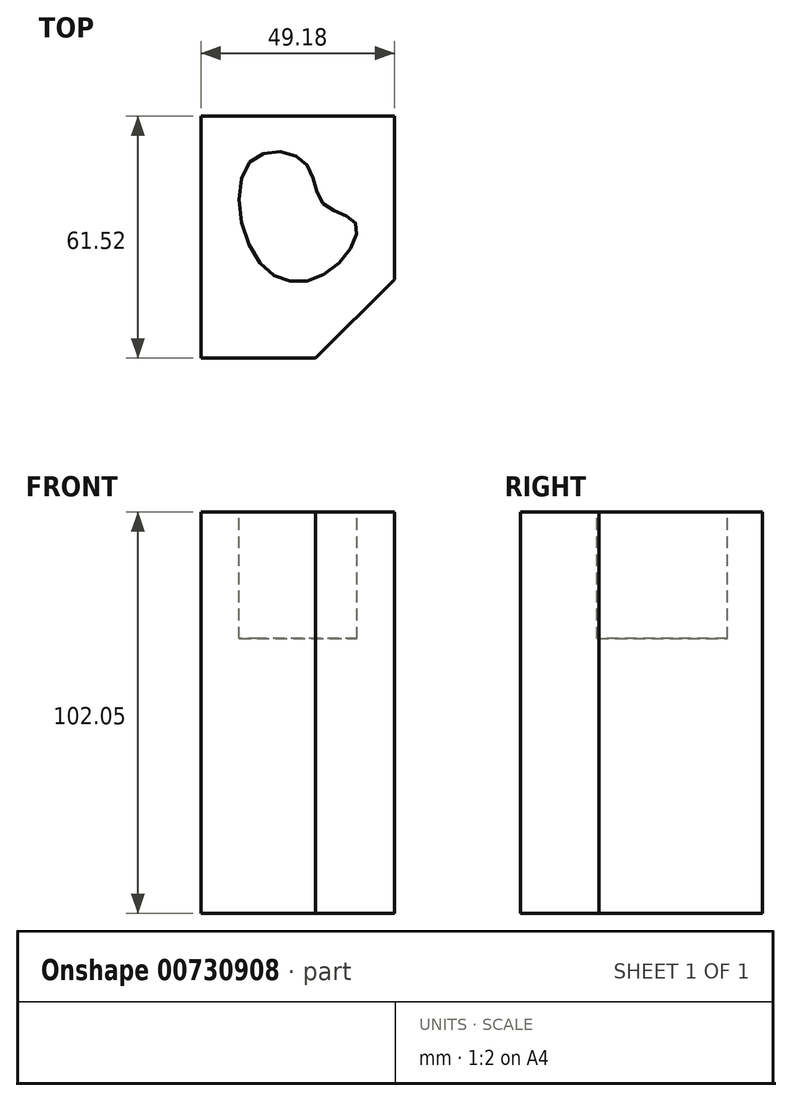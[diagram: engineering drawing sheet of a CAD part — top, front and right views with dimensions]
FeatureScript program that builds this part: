
annotation { "Feature Type Name" : "Feature", "Feature Type Description" : "" }
export const myFeature = defineFeature(function(context is Context, id is Id, definition is map)
    precondition{}
    {
        {
            var Q0;
            Q0=qCreatedBy(makeId("Top.planeOp"),FACE);
            var sketch = newSketch(context, id + "F0", { "sketchPlane" : qUnion([Q0])});
            skLineSegment(sketch, "E0.bottom", {"start": v(0, 0) * mm, "end": v(49.18, 0) * mm});
            skLineSegment(sketch, "E0.top", {"start": v(0, 61.52) * mm, "end": v(49.18, 61.52) * mm});
            skLineSegment(sketch, "E0.left", {"start": v(0, 0) * mm, "end": v(0, 61.52) * mm});
            skLineSegment(sketch, "E0.right", {"start": v(49.18, 0) * mm, "end": v(49.18, 61.52) * mm});
            skSolve(sketch);
        }
        {
            var Q0;
            Q0=makeQuery(id+"F0.imprint","IMPRINT",FACE,{"disambiguationData":[TD([[makeQuery(id+"F0.imprint","IMPRINT",EDGE,{"derivedFrom":sQuery(id+"F0.wireOp",EDGE,"E0.bottom")}),1.0]])]});
            extrude(context, id + "F1", {"entities" : qUnion([Q0]), "depth" : 102.05 * mm, "offsetDistance" : 25 * mm});
        }
        {
            var Q0;
            Q0=makeQuery(id+"F1.opExtrude","SWEPT_EDGE",EDGE,{"disambiguationData":[OSD([sQuery(id+"F0.wireOp",EDGE,"E0.bottom"),sQuery(id+"F0.wireOp",EDGE,"E0.right")])]});
            chamfer(context, id + "F2", {"entities" : qUnion([Q0]), "width" : 20 * mm, "tangentPropagation" : true});
        }
        {
            var Q0;
            Q0=makeQuery(id+"F1.opExtrude","CAP_FACE",FACE,{"disambiguationData":[OSD([sQuery(id+"F0.wireOp",EDGE,"E0.bottom"),sQuery(id+"F0.wireOp",EDGE,"E0.top"),sQuery(id+"F0.wireOp",EDGE,"E0.left"),sQuery(id+"F0.wireOp",EDGE,"E0.right")])],"isStart":false});
            var sketch = newSketch(context, id + "F3", { "sketchPlane" : qUnion([Q0])});
            skFitSpline(sketch, "E1", {"points": [v(14.97, 24.18) * mm, v(12.45, 49.81) * mm, v(26.24, 49.94) * mm, v(31.2, 39.17) * mm, v(39.44, 34.08) * mm, v(31.26, 21.3) * mm, v(14.97, 24.18) * mm]});
            skSolve(sketch);
        }
        {
            var Q0;
            Q0=makeQuery(id+"F3.imprint","IMPRINT",FACE,{"disambiguationData":[TD([[makeQuery(id+"F3.imprint","IMPRINT",EDGE,{"derivedFrom":sQuery(id+"F3.wireOp",EDGE,"E1")}),-1.0]])]});
            extrude(context, id + "F4", {"entities" : qUnion([Q0]), "operationType" : NewBodyOperationType.REMOVE, "oppositeDirection" : true, "depth" : 32.22 * mm, "offsetDistance" : 25 * mm});
        }
    });
